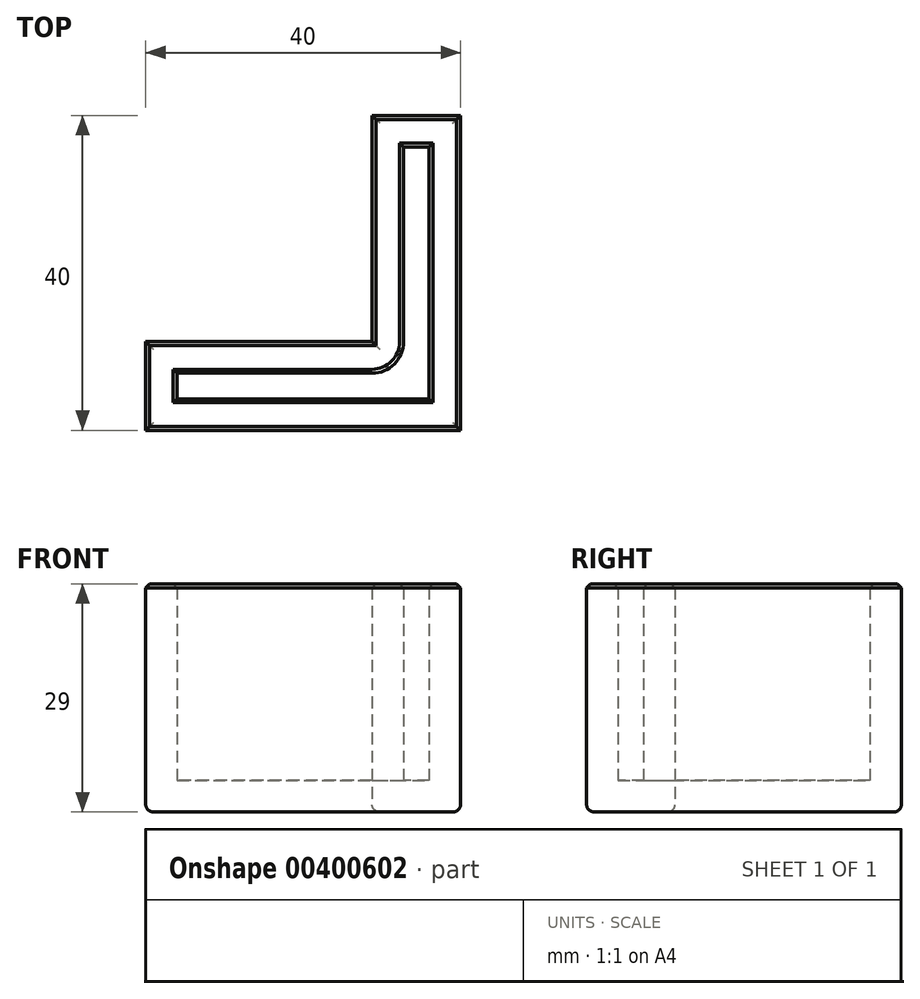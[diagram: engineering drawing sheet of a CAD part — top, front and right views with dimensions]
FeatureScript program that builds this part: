
annotation { "Feature Type Name" : "Feature", "Feature Type Description" : "" }
export const myFeature = defineFeature(function(context is Context, id is Id, definition is map)
    precondition{}
    {
        {
            var Q0;
            Q0=qCreatedBy(makeId("Top.planeOp"),FACE);
            var sketch = newSketch(context, id + "F0", { "sketchPlane" : qUnion([Q0])});
            skLineSegment(sketch, "E0", {"start": v(0, 28.75) * mm, "end": v(0, 4) * mm});
            skLineSegment(sketch, "E1", {"start": v(-4, 0) * mm, "end": v(-28.75, 0) * mm});
            skLineSegment(sketch, "E2", {"start": v(-28.75, 0) * mm, "end": v(-28.75, -3.25) * mm});
            skLineSegment(sketch, "E3", {"start": v(-28.75, -3.25) * mm, "end": v(3.25, -3.25) * mm});
            skLineSegment(sketch, "E4", {"start": v(3.25, -3.25) * mm, "end": v(3.25, 28.75) * mm});
            skLineSegment(sketch, "E5", {"start": v(3.25, 28.75) * mm, "end": v(0, 28.75) * mm});
            skLineSegment(sketch, "E6.0", {"start": v(-32.75, -7.25) * mm, "end": v(7.25, -7.25) * mm});
            skLineSegment(sketch, "E6.1", {"start": v(7.25, 32.75) * mm, "end": v(-4, 32.75) * mm});
            skLineSegment(sketch, "E6.2", {"start": v(-4, 32.75) * mm, "end": v(-4, 4) * mm});
            skLineSegment(sketch, "E6.3", {"start": v(7.25, -7.25) * mm, "end": v(7.25, 32.75) * mm});
            skLineSegment(sketch, "E6.4", {"start": v(-4, 4) * mm, "end": v(-32.75, 4) * mm});
            skLineSegment(sketch, "E6.5", {"start": v(-32.75, 4) * mm, "end": v(-32.75, -7.25) * mm});
            skPoint(sketch, "E7.visualSharp", {"position": v(0, 0) * mm});
            skArc(sketch, "E7.filletArc", {"start": v(-4, 0) * mm, "mid": v(-1.17, 1.17) * mm, "end": v(0, 4) * mm});
            skSolve(sketch);
        }
        {
            var Q0;
            Q0 = qSketchRegion(id + "F0", true);
            extrude(context, id + "F1", {"entities" : qUnion([Q0]), "depth" : 25 * mm});
        }
        {
            var Q0;
            Q0=makeQuery(id+"F1.opExtrude","CAP_FACE",FACE,{"disambiguationData":[OSD([sQuery(id+"F0.wireOp",EDGE,"E0"),sQuery(id+"F0.wireOp",EDGE,"E1"),sQuery(id+"F0.wireOp",EDGE,"E2"),sQuery(id+"F0.wireOp",EDGE,"E3"),sQuery(id+"F0.wireOp",EDGE,"E4"),sQuery(id+"F0.wireOp",EDGE,"E5"),sQuery(id+"F0.wireOp",EDGE,"E6.0"),sQuery(id+"F0.wireOp",EDGE,"E6.1"),sQuery(id+"F0.wireOp",EDGE,"E6.2"),sQuery(id+"F0.wireOp",EDGE,"E6.3"),sQuery(id+"F0.wireOp",EDGE,"E6.4"),sQuery(id+"F0.wireOp",EDGE,"E6.5"),sQuery(id+"F0.wireOp",EDGE,"E7.filletArc")])],"isStart":false});
            chamfer(context, id + "F2", {"entities" : qUnion([Q0]), "width" : 0.5 * mm, "tangentPropagation" : true});
        }
        {
            var Q0;
            Q0=makeQuery(id+"F1.opExtrude","CAP_FACE",FACE,{"disambiguationData":[OSD([sQuery(id+"F0.wireOp",EDGE,"E0"),sQuery(id+"F0.wireOp",EDGE,"E1"),sQuery(id+"F0.wireOp",EDGE,"E2"),sQuery(id+"F0.wireOp",EDGE,"E3"),sQuery(id+"F0.wireOp",EDGE,"E4"),sQuery(id+"F0.wireOp",EDGE,"E5"),sQuery(id+"F0.wireOp",EDGE,"E6.0"),sQuery(id+"F0.wireOp",EDGE,"E6.1"),sQuery(id+"F0.wireOp",EDGE,"E6.2"),sQuery(id+"F0.wireOp",EDGE,"E6.3"),sQuery(id+"F0.wireOp",EDGE,"E6.4"),sQuery(id+"F0.wireOp",EDGE,"E6.5"),sQuery(id+"F0.wireOp",EDGE,"E7.filletArc")])],"isStart":true});
            var sketch = newSketch(context, id + "F3", { "sketchPlane" : qUnion([Q0])});
            skLineSegment(sketch, "E8.0", {"start": v(-32.75, 7.25) * mm, "end": v(7.25, 7.25) * mm});
            skLineSegment(sketch, "E8.1", {"start": v(7.25, 7.25) * mm, "end": v(7.25, -32.75) * mm});
            skLineSegment(sketch, "E8.2", {"start": v(7.25, -32.75) * mm, "end": v(-4, -32.75) * mm});
            skLineSegment(sketch, "E8.3", {"start": v(-4, -32.75) * mm, "end": v(-4, -4) * mm});
            skLineSegment(sketch, "E8.4", {"start": v(-32.75, -4) * mm, "end": v(-32.75, 7.25) * mm});
            skLineSegment(sketch, "E8.5", {"start": v(-4, -4) * mm, "end": v(-32.75, -4) * mm});
            skSolve(sketch);
        }
        {
            var Q0;
            Q0 = qSketchRegion(id + "F3", true);
            extrude(context, id + "F4", {"entities" : qUnion([Q0]), "operationType" : NewBodyOperationType.ADD, "depth" : 4 * mm});
        }
        {
            var Q0;
            Q0=makeQuery(id+"F4.opExtrude","CAP_FACE",FACE,{"disambiguationData":[OSD([sQuery(id+"F3.wireOp",EDGE,"E8.0"),sQuery(id+"F3.wireOp",EDGE,"E8.1"),sQuery(id+"F3.wireOp",EDGE,"E8.2"),sQuery(id+"F3.wireOp",EDGE,"E8.3"),sQuery(id+"F3.wireOp",EDGE,"E8.4"),sQuery(id+"F3.wireOp",EDGE,"E8.5")])],"isStart":false});
            fillet(context, id + "F5", {"entities" : qUnion([Q0]), "radius" : 1 * mm, "tangentPropagation" : true, "allowEdgeOverflow" : false});
        }
    });
